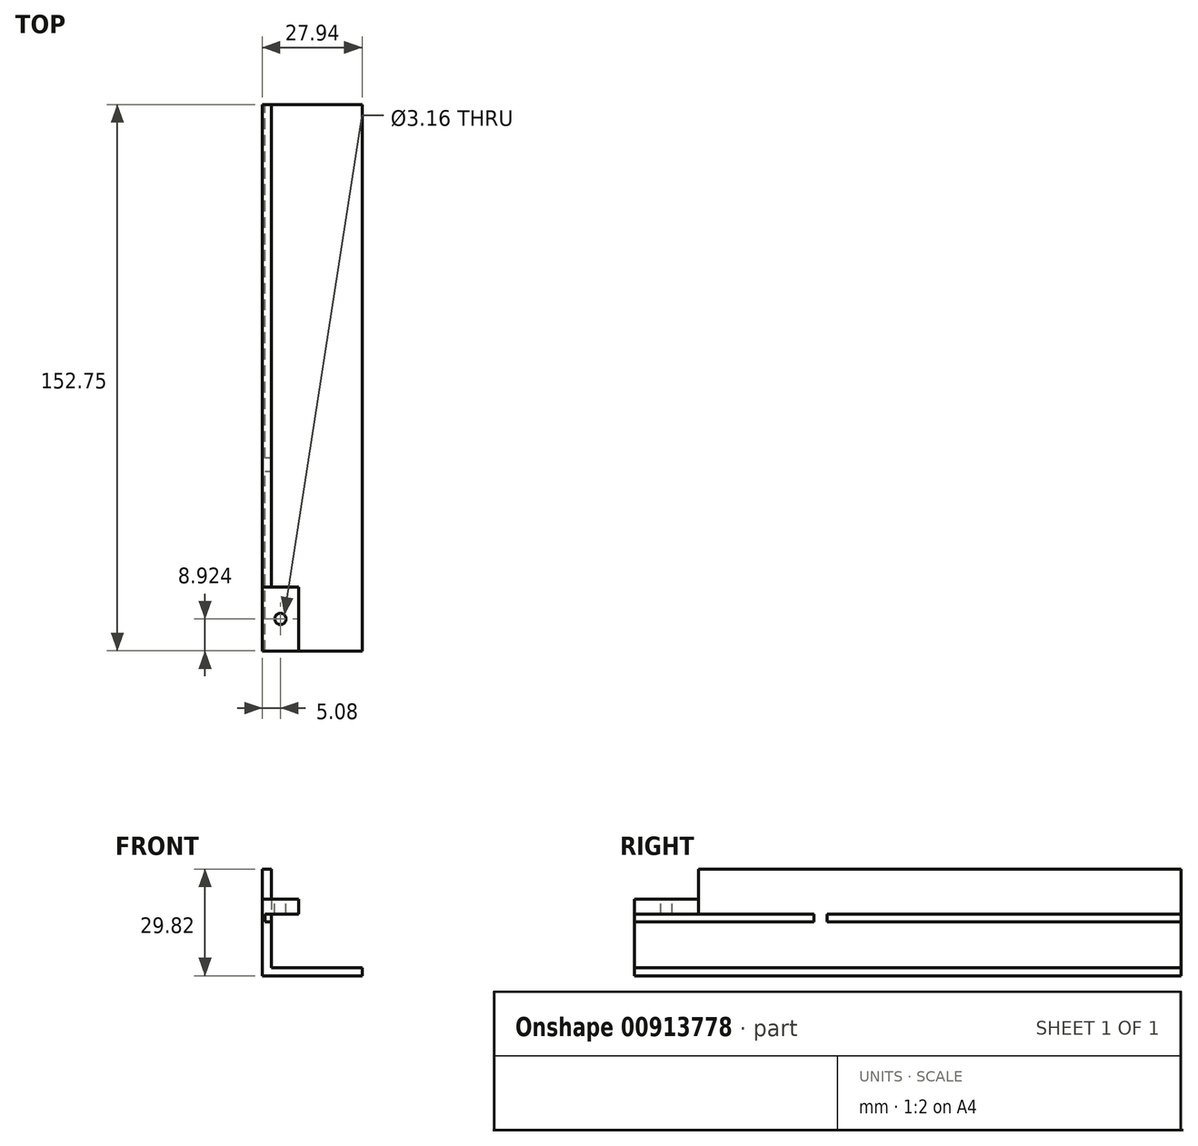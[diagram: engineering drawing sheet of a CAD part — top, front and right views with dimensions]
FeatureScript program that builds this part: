
annotation { "Feature Type Name" : "Feature", "Feature Type Description" : "" }
export const myFeature = defineFeature(function(context is Context, id is Id, definition is map)
    precondition{}
    {
        {
            var Q0;
            Q0=qCreatedBy(makeId("Right.planeOp"),FACE);
            var sketch = newSketch(context, id + "F0", { "sketchPlane" : qUnion([Q0])});
            skLineSegment(sketch, "E0.bottom", {"start": v(-76.26, 12.65) * mm, "end": v(76.49, 12.65) * mm});
            skLineSegment(sketch, "E0.top", {"start": v(-76.26, -17.17) * mm, "end": v(76.49, -17.17) * mm});
            skLineSegment(sketch, "E0.left", {"start": v(-76.26, 12.65) * mm, "end": v(-76.26, -17.17) * mm});
            skLineSegment(sketch, "E0.right", {"start": v(76.49, 12.65) * mm, "end": v(76.49, -17.17) * mm});
            skLineSegment(sketch, "E1.bottom", {"start": v(-76.26, 12.65) * mm, "end": v(-58.41, 12.65) * mm});
            skLineSegment(sketch, "E1.top", {"start": v(-76.26, 4.3) * mm, "end": v(-58.41, 4.3) * mm});
            skLineSegment(sketch, "E1.left", {"start": v(-76.26, 12.65) * mm, "end": v(-76.26, 4.3) * mm});
            skLineSegment(sketch, "E1.right", {"start": v(-58.41, 12.65) * mm, "end": v(-58.41, 4.3) * mm});
            skSolve(sketch);
        }
        {
            var Q0;
            {var subQ1=sQuery(id+"F0.wireOp",EDGE,"E0.top");Q0=makeQuery(id+"F0.imprint","IMPRINT",FACE,{"disambiguationData":[TD([[makeQuery(id+"F0.imprint","IMPRINT",EDGE,{"derivedFrom":subQ1}),1.0]])]});}
            extrude(context, id + "F1", {"entities" : qUnion([Q0]), "depth" : 2.54 * mm, "offsetDistance" : 25.4 * mm});
        }
        {
            var Q0;
            Q0=makeQuery(id+"F1.opExtrude","CAP_FACE",FACE,{"disambiguationData":[OSD([sQuery(id+"F0.wireOp",EDGE,"E0.bottom"),sQuery(id+"F0.wireOp",EDGE,"E0.top"),sQuery(id+"F0.wireOp",EDGE,"E0.left"),sQuery(id+"F0.wireOp",EDGE,"E0.right"),sQuery(id+"F0.wireOp",EDGE,"E1.top"),sQuery(id+"F0.wireOp",EDGE,"E1.right")])],"isStart":false});
            var sketch = newSketch(context, id + "F2", { "sketchPlane" : qUnion([Q0])});
            skLineSegment(sketch, "E2.bottom", {"start": v(-76.26, 4.3) * mm, "end": v(-58.4, 4.3) * mm});
            skLineSegment(sketch, "E2.top", {"start": v(-76.26, 0) * mm, "end": v(-58.4, 0) * mm});
            skLineSegment(sketch, "E2.left", {"start": v(-76.26, 4.3) * mm, "end": v(-76.26, 0) * mm});
            skLineSegment(sketch, "E2.right", {"start": v(-58.4, 4.3) * mm, "end": v(-58.4, 0) * mm});
            skSolve(sketch);
        }
        {
            var Q0;
            Q0=makeQuery(id+"F2.imprint","IMPRINT",FACE,{"disambiguationData":[TD([[makeQuery(id+"F2.imprint","IMPRINT",EDGE,{"derivedFrom":sQuery(id+"F2.wireOp",EDGE,"E2.top")}),1.0]])]});
            extrude(context, id + "F3", {"entities" : qUnion([Q0]), "operationType" : NewBodyOperationType.ADD, "depth" : 7.62 * mm, "offsetDistance" : 25.4 * mm});
        }
        {
            var Q0;
            Q0=makeQuery(id+"F1.opExtrude","CAP_FACE",FACE,{"disambiguationData":[OSD([sQuery(id+"F0.wireOp",EDGE,"E0.bottom"),sQuery(id+"F0.wireOp",EDGE,"E0.top"),sQuery(id+"F0.wireOp",EDGE,"E0.left"),sQuery(id+"F0.wireOp",EDGE,"E0.right"),sQuery(id+"F0.wireOp",EDGE,"E1.top"),sQuery(id+"F0.wireOp",EDGE,"E1.right")])],"isStart":false});
            var sketch = newSketch(context, id + "F4", { "sketchPlane" : qUnion([Q0])});
            skLineSegment(sketch, "E3.bottom", {"start": v(-76.26, -17.17) * mm, "end": v(76.49, -17.17) * mm});
            skLineSegment(sketch, "E3.top", {"start": v(-76.26, -14.96) * mm, "end": v(76.49, -14.96) * mm});
            skLineSegment(sketch, "E3.left", {"start": v(-76.26, -17.17) * mm, "end": v(-76.26, -14.96) * mm});
            skLineSegment(sketch, "E3.right", {"start": v(76.49, -17.17) * mm, "end": v(76.49, -14.96) * mm});
            skSolve(sketch);
        }
        {
            var Q0;
            Q0=makeQuery(id+"F4.imprint","IMPRINT",FACE,{"disambiguationData":[TD([[makeQuery(id+"F4.imprint","IMPRINT",EDGE,{"derivedFrom":sQuery(id+"F4.wireOp",EDGE,"E3.bottom")}),1.0]])]});
            extrude(context, id + "F5", {"entities" : qUnion([Q0]), "operationType" : NewBodyOperationType.ADD, "depth" : 25.4 * mm, "offsetDistance" : 25.4 * mm});
        }
        {
            var Q0;
            Q0=makeQuery(id+"F3.boolean.opBoolean","MERGE",FACE,{"derivedFrom":[makeQuery(id+"F1.opExtrude","SWEPT_FACE",FACE,{"disambiguationData":[OSD([sQuery(id+"F0.wireOp",EDGE,"E1.top")])]}),makeQuery(id+"F3.opExtrude","SWEPT_FACE",FACE,{"disambiguationData":[OSD([sQuery(id+"F2.wireOp",EDGE,"E2.bottom")])]})]});
            var sketch = newSketch(context, id + "F6", { "sketchPlane" : qUnion([Q0])});
            skCircle(sketch, "E4", {"center": v(5.08, -67.34) * mm, "radius": 1.58 * mm});
            skPoint(sketch, "E5", {"position": v(5.08, -76.26) * mm});
            skPoint(sketch, "E6", {"position": v(0, -67.34) * mm});
            skSolve(sketch);
        }
        {
            var Q0;
            Q0=makeQuery(id+"F6.imprint","IMPRINT",FACE,{"disambiguationData":[TD([[makeQuery(id+"F6.imprint","IMPRINT",EDGE,{"derivedFrom":sQuery(id+"F6.wireOp",EDGE,"E4")}),1.0]])]});
            extrude(context, id + "F7", {"entities" : qUnion([Q0]), "operationType" : NewBodyOperationType.REMOVE, "endBound" : BoundingType.UP_TO_NEXT, "oppositeDirection" : true, "depth" : 25.4 * mm, "offsetDistance" : 25.4 * mm});
        }
        {
            var Q0;
            Q0=makeQuery(id+"F1.opExtrude","CAP_FACE",FACE,{"disambiguationData":[OSD([sQuery(id+"F0.wireOp",EDGE,"E0.bottom"),sQuery(id+"F0.wireOp",EDGE,"E0.top"),sQuery(id+"F0.wireOp",EDGE,"E0.left"),sQuery(id+"F0.wireOp",EDGE,"E0.right"),sQuery(id+"F0.wireOp",EDGE,"E1.top"),sQuery(id+"F0.wireOp",EDGE,"E1.right")])],"isStart":false});
            var sketch = newSketch(context, id + "F8", { "sketchPlane" : qUnion([Q0])});
            skLineSegment(sketch, "E7.bottom", {"start": v(-76.26, 0) * mm, "end": v(76.49, 0) * mm});
            skLineSegment(sketch, "E7.top", {"start": v(-76.26, -2.12) * mm, "end": v(76.49, -2.12) * mm});
            skLineSegment(sketch, "E7.left", {"start": v(-76.26, 0) * mm, "end": v(-76.26, -2.12) * mm});
            skLineSegment(sketch, "E7.right", {"start": v(76.49, 0) * mm, "end": v(76.49, -2.12) * mm});
            skSolve(sketch);
        }
        {
            var Q0;
            Q0 = qSketchRegion(id + "F8", true);
            extrude(context, id + "F9", {"entities" : qUnion([Q0]), "operationType" : NewBodyOperationType.REMOVE, "oppositeDirection" : true, "depth" : 1.78 * mm, "offsetDistance" : 25.4 * mm});
        }
        {
            var Q0;
            Q0=makeQuery(id+"F9.boolean.opBoolean","COPY",FACE,{"derivedFrom":makeQuery(id+"F9.opExtrude","CAP_FACE",FACE,{"disambiguationData":[OSD([sQuery(id+"F8.wireOp",EDGE,"E7.bottom"),sQuery(id+"F8.wireOp",EDGE,"E7.top"),sQuery(id+"F8.wireOp",EDGE,"E7.left"),sQuery(id+"F8.wireOp",EDGE,"E7.right")])],"isStart":false})});
            var sketch = newSketch(context, id + "F10", { "sketchPlane" : qUnion([Q0])});
            skLineSegment(sketch, "E8.bottom", {"start": v(-26.15, 0) * mm, "end": v(-22.4, 0) * mm});
            skLineSegment(sketch, "E8.top", {"start": v(-26.15, -2.12) * mm, "end": v(-22.4, -2.12) * mm});
            skLineSegment(sketch, "E8.left", {"start": v(-26.15, 0) * mm, "end": v(-26.15, -2.12) * mm});
            skLineSegment(sketch, "E8.right", {"start": v(-22.4, 0) * mm, "end": v(-22.4, -2.12) * mm});
            skSolve(sketch);
        }
        {
            var Q0;
            Q0=makeQuery(id+"F10.imprint","IMPRINT",FACE,{"disambiguationData":[TD([[makeQuery(id+"F10.imprint","IMPRINT",EDGE,{"derivedFrom":sQuery(id+"F10.wireOp",EDGE,"E8.bottom")}),-1.0]])]});
            extrude(context, id + "F11", {"entities" : qUnion([Q0]), "operationType" : NewBodyOperationType.ADD, "depth" : 1.78 * mm, "offsetDistance" : 25.4 * mm});
        }
    });
